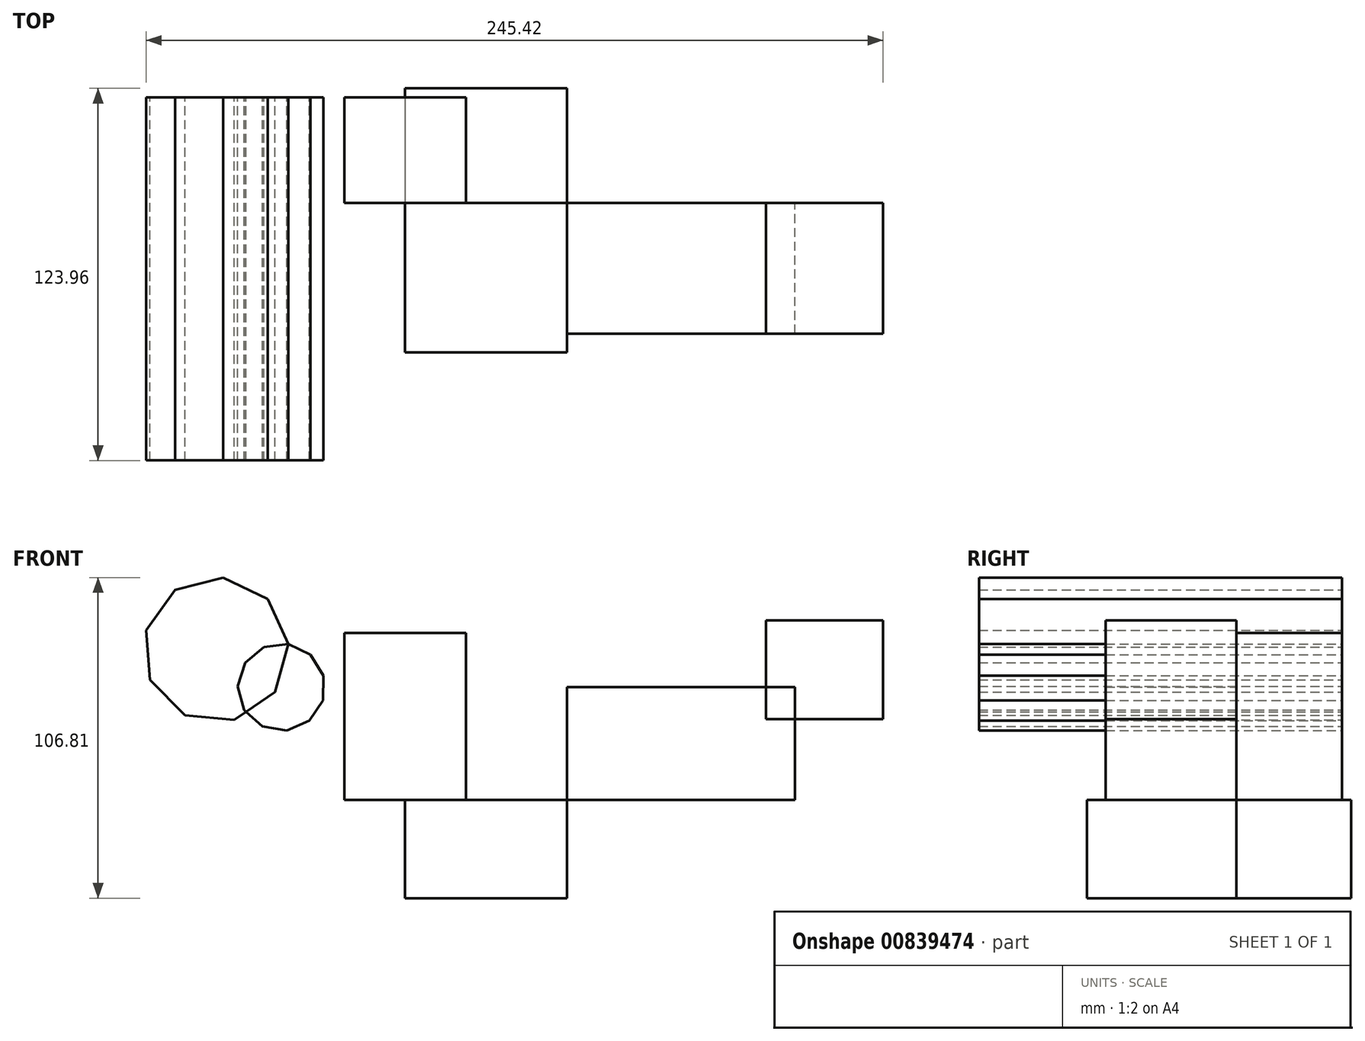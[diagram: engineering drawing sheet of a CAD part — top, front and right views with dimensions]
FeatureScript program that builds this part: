
annotation { "Feature Type Name" : "Feature", "Feature Type Description" : "" }
export const myFeature = defineFeature(function(context is Context, id is Id, definition is map)
    precondition{}
    {
        {
            var Q0;
            Q0=qCreatedBy(makeId("Front.planeOp"),FACE);
            var sketch = newSketch(context, id + "F0", { "sketchPlane" : qUnion([Q0])});
            skCircle(sketch, "E0.cCircle", {"center": v(-21.73, 12.46) * mm, "radius": 24.16 * mm, "construction": true});
            skLineSegment(sketch, "E0.0", {"start": v(-15.68, -10.94) * mm, "end": v(-32.14, -9.35) * mm});
            skLineSegment(sketch, "E0.1", {"start": v(-32.14, -9.35) * mm, "end": v(-43.72, 2.45) * mm});
            skLineSegment(sketch, "E0.2", {"start": v(-43.72, 2.45) * mm, "end": v(-45.01, 18.92) * mm});
            skLineSegment(sketch, "E0.3", {"start": v(-45.01, 18.92) * mm, "end": v(-35.4, 32.38) * mm});
            skLineSegment(sketch, "E0.4", {"start": v(-35.4, 32.38) * mm, "end": v(-19.4, 36.51) * mm});
            skLineSegment(sketch, "E0.5", {"start": v(-19.4, 36.51) * mm, "end": v(-4.49, 29.4) * mm});
            skLineSegment(sketch, "E0.6", {"start": v(-4.49, 29.4) * mm, "end": v(2.36, 14.35) * mm});
            skLineSegment(sketch, "E0.7", {"start": v(2.36, 14.35) * mm, "end": v(-2.06, -1.58) * mm});
            skLineSegment(sketch, "E0.8", {"start": v(-2.06, -1.58) * mm, "end": v(-15.68, -10.94) * mm});
            skCircle(sketch, "E1.cCircle", {"center": v(0, 0) * mm, "radius": 14.54 * mm, "construction": true});
            skLineSegment(sketch, "E1.0", {"start": v(2.36, 14.35) * mm, "end": v(9.75, 10.8) * mm});
            skLineSegment(sketch, "E1.1", {"start": v(9.75, 10.8) * mm, "end": v(14.03, 3.81) * mm});
            skLineSegment(sketch, "E1.2", {"start": v(14.03, 3.81) * mm, "end": v(13.87, -4.38) * mm});
            skLineSegment(sketch, "E1.3", {"start": v(13.87, -4.38) * mm, "end": v(9.3, -11.18) * mm});
            skLineSegment(sketch, "E1.4", {"start": v(9.3, -11.18) * mm, "end": v(1.78, -14.43) * mm});
            skLineSegment(sketch, "E1.5", {"start": v(1.78, -14.43) * mm, "end": v(-6.3, -13.1) * mm});
            skLineSegment(sketch, "E1.6", {"start": v(-6.3, -13.1) * mm, "end": v(-12.4, -7.61) * mm});
            skLineSegment(sketch, "E1.7", {"start": v(-12.4, -7.61) * mm, "end": v(-14.54, 0.3) * mm});
            skLineSegment(sketch, "E1.8", {"start": v(-14.54, 0.3) * mm, "end": v(-12.07, 8.11) * mm});
            skLineSegment(sketch, "E1.9", {"start": v(-12.07, 8.11) * mm, "end": v(-5.77, 13.35) * mm});
            skLineSegment(sketch, "E1.10", {"start": v(-5.77, 13.35) * mm, "end": v(2.36, 14.35) * mm});
            skSolve(sketch);
        }
        {
            var Q0;
            {var subQ2=sQuery(id+"F0.wireOp",EDGE,"E0.0");Q0=makeQuery(id+"F0.imprint","IMPRINT",FACE,{"disambiguationData":[TD([[makeQuery(id+"F0.imprint","IMPRINT",EDGE,{"derivedFrom":subQ2}),-1.0]])]});}
            var Q1;
            {var subQ1=sQuery(id+"F0.wireOp",EDGE,"E0.7");Q1=makeQuery(id+"F0.imprint","IMPRINT",FACE,{"disambiguationData":[TD([[makeQuery(id+"F0.imprint","IMPRINT",EDGE,{"derivedFrom":subQ1}),1.0]])]});}
            extrude(context, id + "F1", {"entities" : qUnion([Q0, Q1]), "depth" : 120.99 * mm, "offsetDistance" : 25.4 * mm});
        }
        {
            var Q0;
            Q0=qCreatedBy(makeId("Front.planeOp"),FACE);
            var sketch = newSketch(context, id + "F2", { "sketchPlane" : qUnion([Q0])});
            skLineSegment(sketch, "E2.bottom", {"start": v(20.96, 18.1) * mm, "end": v(61.56, 18.1) * mm});
            skLineSegment(sketch, "E2.top", {"start": v(20.96, -37.57) * mm, "end": v(61.56, -37.57) * mm});
            skLineSegment(sketch, "E2.left", {"start": v(20.96, 18.1) * mm, "end": v(20.96, -37.57) * mm});
            skLineSegment(sketch, "E2.right", {"start": v(61.56, 18.1) * mm, "end": v(61.56, -37.57) * mm});
            skSolve(sketch);
        }
        {
            var Q0;
            Q0=makeQuery(id+"F2.imprint","IMPRINT",FACE,{"disambiguationData":[TD([[makeQuery(id+"F2.imprint","IMPRINT",EDGE,{"derivedFrom":sQuery(id+"F2.wireOp",EDGE,"E2.bottom")}),-1.0]])]});
            extrude(context, id + "F3", {"entities" : qUnion([Q0]), "depth" : 35.25 * mm, "offsetDistance" : 25.4 * mm});
        }
        {
            var Q0;
            Q0=makeQuery(id+"F3.opExtrude","CAP_FACE",FACE,{"disambiguationData":[OSD([sQuery(id+"F2.wireOp",EDGE,"E2.bottom"),sQuery(id+"F2.wireOp",EDGE,"E2.top"),sQuery(id+"F2.wireOp",EDGE,"E2.left"),sQuery(id+"F2.wireOp",EDGE,"E2.right")])],"isStart":false});
            var sketch = newSketch(context, id + "F4", { "sketchPlane" : qUnion([Q0])});
            skLineSegment(sketch, "E3.bottom", {"start": v(41.26, -37.57) * mm, "end": v(95.12, -37.57) * mm});
            skLineSegment(sketch, "E3.top", {"start": v(41.26, -70.3) * mm, "end": v(95.12, -70.3) * mm});
            skLineSegment(sketch, "E3.left", {"start": v(41.26, -37.57) * mm, "end": v(41.26, -70.3) * mm});
            skLineSegment(sketch, "E3.right", {"start": v(95.12, -37.57) * mm, "end": v(95.12, -70.3) * mm});
            skSolve(sketch);
        }
        {
            var Q0;
            Q0=makeQuery(id+"F4.imprint","IMPRINT",FACE,{"disambiguationData":[TD([[makeQuery(id+"F4.imprint","IMPRINT",EDGE,{"derivedFrom":sQuery(id+"F4.wireOp",EDGE,"E3.top")}),1.0]])]});
            extrude(context, id + "F5", {"entities" : qUnion([Q0]), "depth" : 49.8 * mm, "offsetDistance" : 25.4 * mm});
        }
        {
            var Q0;
            Q0=makeQuery(id+"F5.opExtrude","CAP_FACE",FACE,{"disambiguationData":[OSD([sQuery(id+"F4.wireOp",EDGE,"E3.bottom"),sQuery(id+"F4.wireOp",EDGE,"E3.top"),sQuery(id+"F4.wireOp",EDGE,"E3.left"),sQuery(id+"F4.wireOp",EDGE,"E3.right")])],"isStart":true});
            var sketch = newSketch(context, id + "F6", { "sketchPlane" : qUnion([Q0])});
            skLineSegment(sketch, "E4.bottom", {"start": v(-171.13, 0) * mm, "end": v(-95.12, 0) * mm});
            skLineSegment(sketch, "E4.top", {"start": v(-171.13, -37.57) * mm, "end": v(-95.12, -37.57) * mm});
            skLineSegment(sketch, "E4.left", {"start": v(-171.13, 0) * mm, "end": v(-171.13, -37.57) * mm});
            skLineSegment(sketch, "E4.right", {"start": v(-95.12, 0) * mm, "end": v(-95.12, -37.57) * mm});
            skLineSegment(sketch, "E5.bottom", {"start": v(-161.47, -10.67) * mm, "end": v(-200.4, -10.67) * mm});
            skLineSegment(sketch, "E5.top", {"start": v(-161.47, 22.24) * mm, "end": v(-200.4, 22.24) * mm});
            skLineSegment(sketch, "E5.left", {"start": v(-161.47, -10.67) * mm, "end": v(-161.47, 22.24) * mm});
            skLineSegment(sketch, "E5.right", {"start": v(-200.4, -10.67) * mm, "end": v(-200.4, 22.24) * mm});
            skSolve(sketch);
        }
        {
            var Q0;
            {var subQ2=sQuery(id+"F6.wireOp",EDGE,"E4.top");Q0=makeQuery(id+"F6.imprint","IMPRINT",FACE,{"disambiguationData":[TD([[makeQuery(id+"F6.imprint","IMPRINT",EDGE,{"derivedFrom":subQ2}),1.0]])]});}
            var Q1;
            {var subQ4=sQuery(id+"F6.wireOp",EDGE,"E5.top");Q1=makeQuery(id+"F6.imprint","IMPRINT",FACE,{"disambiguationData":[TD([[makeQuery(id+"F6.imprint","IMPRINT",EDGE,{"derivedFrom":subQ4}),1.0]])]});}
            extrude(context, id + "F7", {"entities" : qUnion([Q0, Q1]), "oppositeDirection" : true, "depth" : 43.48 * mm, "offsetDistance" : 25.4 * mm});
        }
        {
            var Q0;
            Q0=makeQuery(id+"F5.opExtrude","CAP_FACE",FACE,{"disambiguationData":[OSD([sQuery(id+"F4.wireOp",EDGE,"E3.bottom"),sQuery(id+"F4.wireOp",EDGE,"E3.top"),sQuery(id+"F4.wireOp",EDGE,"E3.left"),sQuery(id+"F4.wireOp",EDGE,"E3.right")])],"isStart":true});
            extrude(context, id + "F8", {"entities" : qUnion([Q0]), "depth" : 38.22 * mm, "offsetDistance" : 25.4 * mm});
        }
    });
